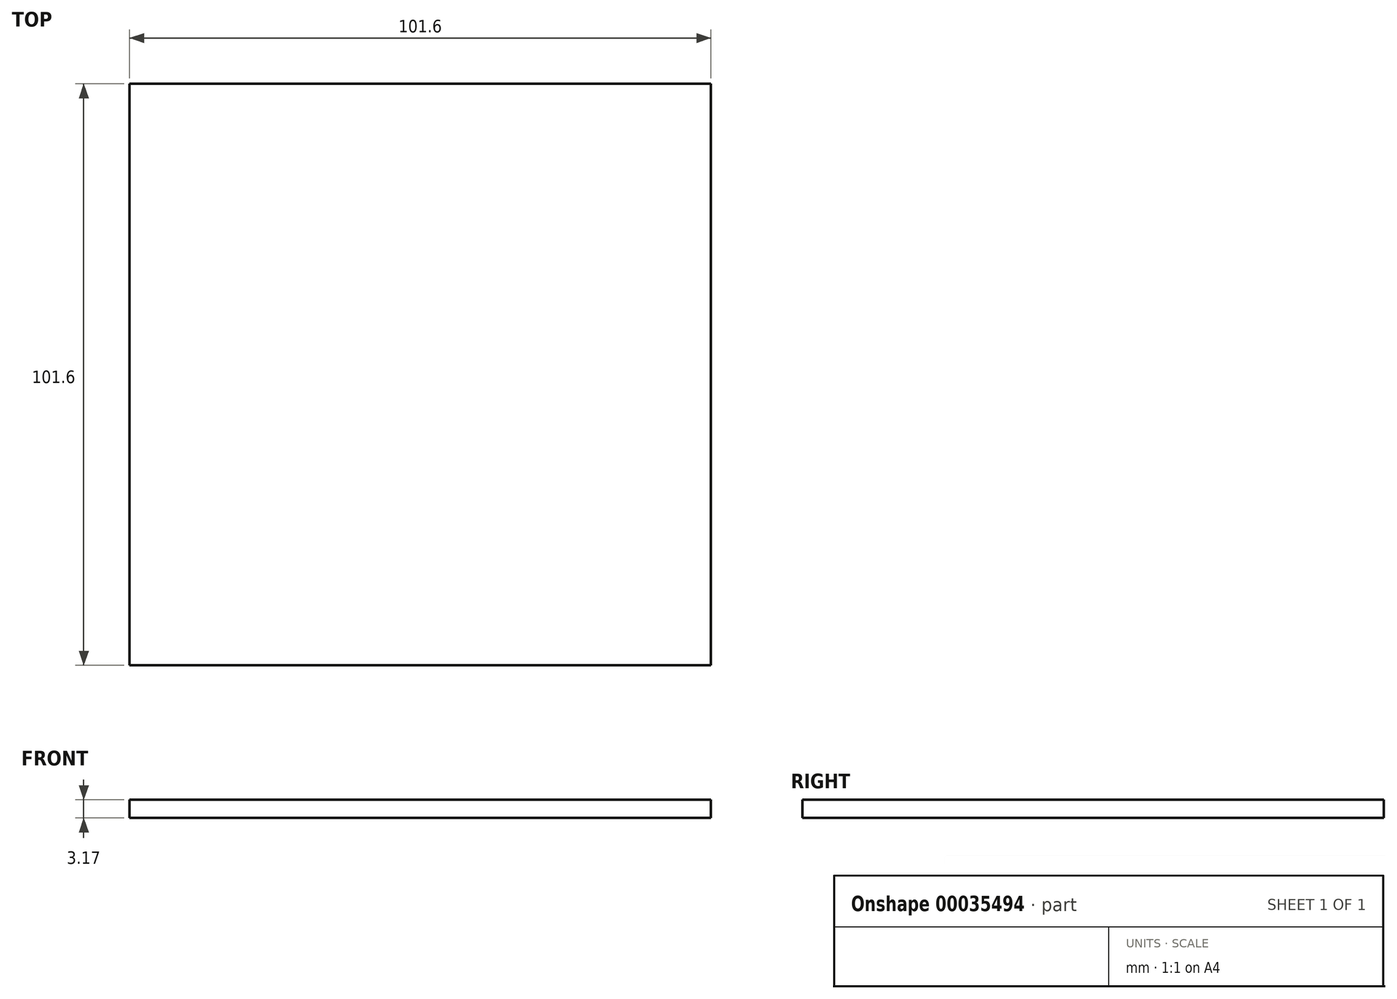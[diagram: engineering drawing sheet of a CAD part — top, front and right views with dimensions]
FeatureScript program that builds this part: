
annotation { "Feature Type Name" : "Feature", "Feature Type Description" : "" }
export const myFeature = defineFeature(function(context is Context, id is Id, definition is map)
    precondition{}
    {
        {
            var Q0;
            Q0=qCreatedBy(makeId("Top.planeOp"),FACE);
            var sketch = newSketch(context, id + "F0", { "sketchPlane" : qUnion([Q0])});
            skLineSegment(sketch, "E0.rect.bottom", {"start": v(50.8, 50.8) * mm, "end": v(-50.8, 50.8) * mm});
            skLineSegment(sketch, "E0.rect.top", {"start": v(50.8, -50.8) * mm, "end": v(-50.8, -50.8) * mm});
            skLineSegment(sketch, "E0.rect.left", {"start": v(50.8, 50.8) * mm, "end": v(50.8, -50.8) * mm});
            skLineSegment(sketch, "E0.rect.right", {"start": v(-50.8, 50.8) * mm, "end": v(-50.8, -50.8) * mm});
            skPoint(sketch, "E0.rect.middle", {"position": v(0, 0) * mm});
            skSolve(sketch);
        }
        {
            var Q0;
            Q0=makeQuery(id+"F0.imprint","IMPRINT",FACE,{"disambiguationData":[TD([[makeQuery(id+"F0.imprint","IMPRINT",EDGE,{"derivedFrom":sQuery(id+"F0.wireOp",EDGE,"E0.rect.bottom")}),1.0]])]});
            extrude(context, id + "F1", {"entities" : qUnion([Q0]), "depth" : 3.17 * mm});
        }
    });
